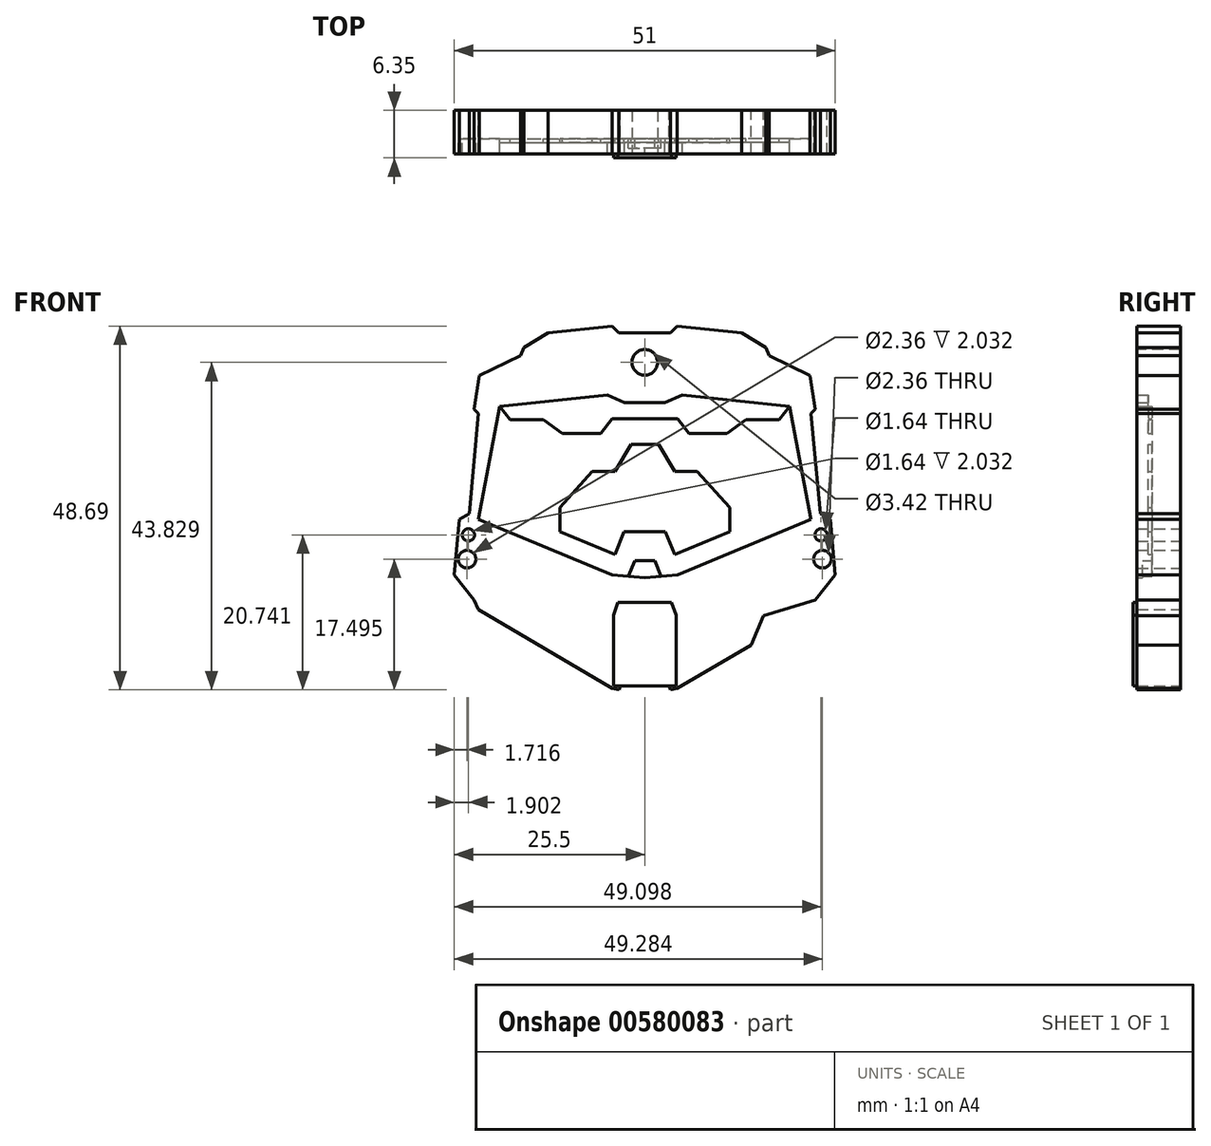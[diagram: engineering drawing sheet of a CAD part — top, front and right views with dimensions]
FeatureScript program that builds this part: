
annotation { "Feature Type Name" : "Feature", "Feature Type Description" : "" }
export const myFeature = defineFeature(function(context is Context, id is Id, definition is map)
    precondition{}
    {
        {
            var Q0;
            Q0=qCreatedBy(makeId("Front.planeOp"),FACE);
            var sketch = newSketch(context, id + "F0", { "sketchPlane" : qUnion([Q0])});
            skLineSegment(sketch, "E0", {"start": v(0, 26.6) * mm, "end": v(0, -24.2) * mm, "construction": true});
            skLineSegment(sketch, "E1", {"start": v(0, 26.6) * mm, "end": v(3.47, 26.6) * mm});
            skLineSegment(sketch, "E2", {"start": v(3.47, 26.6) * mm, "end": v(4.35, 27.52) * mm});
            skLineSegment(sketch, "E3", {"start": v(4.35, 27.52) * mm, "end": v(12.96, 26.6) * mm});
            skLineSegment(sketch, "E4", {"start": v(12.96, 26.6) * mm, "end": v(16.19, 24.61) * mm});
            skLineSegment(sketch, "E5", {"start": v(16.19, 24.61) * mm, "end": v(16.63, 23.54) * mm});
            skLineSegment(sketch, "E6", {"start": v(16.63, 23.54) * mm, "end": v(22.14, 20.88) * mm});
            skLineSegment(sketch, "E7", {"start": v(22.14, 20.88) * mm, "end": v(22.83, 16.39) * mm});
            skLineSegment(sketch, "E8", {"start": v(22.83, 16.39) * mm, "end": v(22.26, 15.82) * mm});
            skLineSegment(sketch, "E9", {"start": v(22.26, 15.82) * mm, "end": v(23.5, 2.4) * mm});
            skLineSegment(sketch, "E10", {"start": v(23.5, 2.4) * mm, "end": v(24.82, 1.66) * mm});
            skLineSegment(sketch, "E11", {"start": v(24.82, 1.66) * mm, "end": v(25.5, -5.75) * mm});
            skLineSegment(sketch, "E12", {"start": v(25.5, -5.75) * mm, "end": v(22.83, -9.12) * mm});
            skLineSegment(sketch, "E13", {"start": v(22.83, -9.12) * mm, "end": v(22.26, -10.43) * mm});
            skLineSegment(sketch, "E14", {"start": v(22.26, -10.43) * mm, "end": v(4.35, -20.92) * mm});
            skLineSegment(sketch, "E15", {"start": v(4.35, -20.92) * mm, "end": v(3.42, -21.17) * mm});
            skLineSegment(sketch, "E16", {"start": v(3.42, -21.17) * mm, "end": v(3.28, -20.63) * mm});
            skLineSegment(sketch, "E17", {"start": v(3.28, -20.63) * mm, "end": v(0, -20.63) * mm});
            skLineSegment(sketch, "E18.MirrorCS", {"start": v(-4.35, -20.92) * mm, "end": v(-3.42, -21.17) * mm});
            skLineSegment(sketch, "E19.MirrorCS", {"start": v(-3.42, -21.17) * mm, "end": v(-3.28, -20.63) * mm});
            skLineSegment(sketch, "E20.MirrorCS", {"start": v(-22.83, -9.12) * mm, "end": v(-22.26, -10.43) * mm});
            skLineSegment(sketch, "E21.MirrorCS", {"start": v(-23.5, 2.4) * mm, "end": v(-24.82, 1.66) * mm});
            skLineSegment(sketch, "E22.MirrorCS", {"start": v(-3.47, 26.6) * mm, "end": v(-4.35, 27.52) * mm});
            skLineSegment(sketch, "E23.MirrorCS", {"start": v(-16.19, 24.61) * mm, "end": v(-16.63, 23.54) * mm});
            skLineSegment(sketch, "E24.MirrorCS", {"start": v(-22.83, 16.39) * mm, "end": v(-22.26, 15.82) * mm});
            skLineSegment(sketch, "E25.MirrorCS", {"start": v(-22.26, -10.43) * mm, "end": v(-4.35, -20.92) * mm});
            skLineSegment(sketch, "E26.MirrorCS", {"start": v(-25.5, -5.75) * mm, "end": v(-22.83, -9.12) * mm});
            skLineSegment(sketch, "E27.MirrorCS", {"start": v(-24.82, 1.66) * mm, "end": v(-25.5, -5.75) * mm});
            skLineSegment(sketch, "E28.MirrorCS", {"start": v(-22.26, 15.82) * mm, "end": v(-23.5, 2.4) * mm});
            skLineSegment(sketch, "E29.MirrorCS", {"start": v(-4.35, 27.52) * mm, "end": v(-12.96, 26.6) * mm});
            skLineSegment(sketch, "E30.MirrorCS", {"start": v(-12.96, 26.6) * mm, "end": v(-16.19, 24.61) * mm});
            skLineSegment(sketch, "E31.MirrorCS", {"start": v(-16.63, 23.54) * mm, "end": v(-22.14, 20.88) * mm});
            skLineSegment(sketch, "E32.MirrorCS", {"start": v(-22.14, 20.88) * mm, "end": v(-22.83, 16.39) * mm});
            skLineSegment(sketch, "E33.MirrorCS", {"start": v(0, 26.6) * mm, "end": v(-3.47, 26.6) * mm});
            skLineSegment(sketch, "E34.MirrorCS", {"start": v(-3.28, -20.63) * mm, "end": v(0, -20.63) * mm});
            skLineSegment(sketch, "E35", {"start": v(-14.22, -15.15) * mm, "end": v(-15.87, -11.25) * mm});
            skLineSegment(sketch, "E36", {"start": v(-15.87, -11.25) * mm, "end": v(-22.83, -9.12) * mm});
            skLineSegment(sketch, "E37", {"start": v(-24.82, 1.66) * mm, "end": v(24.82, 1.66) * mm, "construction": true});
            skLineSegment(sketch, "E38", {"start": v(-22.14, 20.88) * mm, "end": v(-5, 22.7) * mm});
            skLineSegment(sketch, "E39", {"start": v(-5, 22.7) * mm, "end": v(-2.7, 21.68) * mm});
            skLineSegment(sketch, "E40", {"start": v(-2.7, 21.68) * mm, "end": v(0, 21.68) * mm});
            skLineSegment(sketch, "E41", {"start": v(-22.83, 16.39) * mm, "end": v(-5, 18.28) * mm});
            skLineSegment(sketch, "E42", {"start": v(-5, 18.28) * mm, "end": v(-2.7, 17.27) * mm});
            skLineSegment(sketch, "E43", {"start": v(-2.7, 17.27) * mm, "end": v(0, 17.27) * mm});
            skLineSegment(sketch, "E44", {"start": v(-19.4, 16.75) * mm, "end": v(-22.26, 1.66) * mm});
            skLineSegment(sketch, "E45", {"start": v(-22.26, 1.66) * mm, "end": v(-4.4, -5.75) * mm});
            skLineSegment(sketch, "E46", {"start": v(-4.4, -5.75) * mm, "end": v(0, -6.16) * mm});
            skLineSegment(sketch, "E47", {"start": v(-2.2, -5.96) * mm, "end": v(-1.33, -3.87) * mm});
            skLineSegment(sketch, "E48", {"start": v(-1.33, -3.87) * mm, "end": v(0, -3.87) * mm});
            skLineSegment(sketch, "E49", {"start": v(-4.35, -20.92) * mm, "end": v(-4.18, -20.63) * mm});
            skLineSegment(sketch, "E50", {"start": v(-4.18, -20.63) * mm, "end": v(-3.28, -20.63) * mm});
            skLineSegment(sketch, "E51", {"start": v(-12.03, -15.15) * mm, "end": v(-6.88, -10.3) * mm});
            skLineSegment(sketch, "E52", {"start": v(-6.88, -10.3) * mm, "end": v(-4.18, -11.2) * mm});
            skLineSegment(sketch, "E53", {"start": v(-4.18, -11.2) * mm, "end": v(-4.18, -20.63) * mm});
            skLineSegment(sketch, "E54", {"start": v(-4.18, -11.2) * mm, "end": v(-3.6, -9.47) * mm});
            skLineSegment(sketch, "E55", {"start": v(-3.6, -9.47) * mm, "end": v(0, -9.47) * mm});
            skLineSegment(sketch, "E56", {"start": v(-3.6, -9.47) * mm, "end": v(-6.5, -8.26) * mm});
            skLineSegment(sketch, "E57", {"start": v(-23.5, 2.4) * mm, "end": v(-22.26, 1.66) * mm});
            skLineSegment(sketch, "E58", {"start": v(-24.82, 1.66) * mm, "end": v(-22.26, 1.66) * mm});
            skLineSegment(sketch, "E59", {"start": v(-22.26, 1.66) * mm, "end": v(-22.26, -6.84) * mm});
            skLineSegment(sketch, "E60", {"start": v(-22.26, -6.84) * mm, "end": v(-22.83, -9.12) * mm});
            skCircle(sketch, "E61", {"center": v(-23.6, -0.43) * mm, "radius": 0.82 * mm});
            skCircle(sketch, "E62", {"center": v(-23.78, -3.68) * mm, "radius": 1.18 * mm});
            skLineSegment(sketch, "E63", {"start": v(-19.4, 16.75) * mm, "end": v(-18.01, 15.01) * mm});
            skLineSegment(sketch, "E64", {"start": v(-18.01, 15.01) * mm, "end": v(-13.57, 15.01) * mm});
            skLineSegment(sketch, "E65", {"start": v(-13.57, 15.01) * mm, "end": v(-11.01, 13.13) * mm});
            skLineSegment(sketch, "E66", {"start": v(-11.01, 13.13) * mm, "end": v(-5.9, 13.13) * mm});
            skLineSegment(sketch, "E67", {"start": v(-5.9, 13.13) * mm, "end": v(-4.4, 15.09) * mm});
            skLineSegment(sketch, "E68", {"start": v(-4.4, 15.09) * mm, "end": v(0, 15.09) * mm});
            skLineSegment(sketch, "E69", {"start": v(-4.02, -3.05) * mm, "end": v(-2.75, 0) * mm});
            skLineSegment(sketch, "E70", {"start": v(-2.75, 0) * mm, "end": v(0, 0) * mm});
            skLineSegment(sketch, "E71", {"start": v(-4.02, -3.05) * mm, "end": v(-11.36, 0) * mm});
            skLineSegment(sketch, "E72", {"start": v(-11.36, 0) * mm, "end": v(-11.36, 3.27) * mm});
            skLineSegment(sketch, "E73", {"start": v(-11.36, 3.27) * mm, "end": v(-7.03, 8.09) * mm});
            skLineSegment(sketch, "E74", {"start": v(-7.03, 8.09) * mm, "end": v(-4.02, 8.09) * mm});
            skLineSegment(sketch, "E75", {"start": v(-4.02, 8.09) * mm, "end": v(-1.83, 11.7) * mm});
            skLineSegment(sketch, "E76", {"start": v(-1.83, 11.7) * mm, "end": v(0, 11.7) * mm});
            skLineSegment(sketch, "E77.MirrorCS", {"start": v(4.35, -20.92) * mm, "end": v(4.18, -20.63) * mm});
            skLineSegment(sketch, "E78.MirrorCS", {"start": v(4.18, -20.63) * mm, "end": v(3.28, -20.63) * mm});
            skLineSegment(sketch, "E79.MirrorCS", {"start": v(24.82, 1.66) * mm, "end": v(22.26, 1.66) * mm});
            skLineSegment(sketch, "E80.MirrorCS", {"start": v(23.5, 2.4) * mm, "end": v(22.26, 1.66) * mm});
            skLineSegment(sketch, "E81.MirrorCS", {"start": v(22.26, -6.84) * mm, "end": v(22.83, -9.12) * mm});
            skLineSegment(sketch, "E82.MirrorCS", {"start": v(4.18, -11.2) * mm, "end": v(3.6, -9.47) * mm});
            skLineSegment(sketch, "E83.MirrorCS", {"start": v(3.6, -9.47) * mm, "end": v(0, -9.47) * mm});
            skLineSegment(sketch, "E84.MirrorCS", {"start": v(5, 18.28) * mm, "end": v(2.7, 17.27) * mm});
            skLineSegment(sketch, "E85.MirrorCS", {"start": v(7.03, 8.09) * mm, "end": v(4.02, 8.09) * mm});
            skLineSegment(sketch, "E86.MirrorCS", {"start": v(5.9, 13.13) * mm, "end": v(4.4, 15.09) * mm});
            skLineSegment(sketch, "E87.MirrorCS", {"start": v(2.75, 0) * mm, "end": v(0, 0) * mm});
            skLineSegment(sketch, "E88.MirrorCS", {"start": v(5, 22.7) * mm, "end": v(2.7, 21.68) * mm});
            skLineSegment(sketch, "E89.MirrorCS", {"start": v(19.4, 16.75) * mm, "end": v(18.01, 15.01) * mm});
            skLineSegment(sketch, "E90.MirrorCS", {"start": v(4.4, 15.09) * mm, "end": v(0, 15.09) * mm});
            skLineSegment(sketch, "E91.MirrorCS", {"start": v(6.88, -10.3) * mm, "end": v(4.18, -11.2) * mm});
            skLineSegment(sketch, "E92.MirrorCS", {"start": v(18.01, 15.01) * mm, "end": v(13.57, 15.01) * mm});
            skLineSegment(sketch, "E93.MirrorCS", {"start": v(4.4, -5.75) * mm, "end": v(0, -6.16) * mm});
            skLineSegment(sketch, "E94.MirrorCS", {"start": v(4.02, -3.05) * mm, "end": v(2.75, 0) * mm});
            skLineSegment(sketch, "E95.MirrorCS", {"start": v(11.36, 0) * mm, "end": v(11.36, 3.27) * mm});
            skLineSegment(sketch, "E96.MirrorCS", {"start": v(3.6, -9.47) * mm, "end": v(6.5, -8.26) * mm});
            skLineSegment(sketch, "E97.MirrorCS", {"start": v(2.7, 21.68) * mm, "end": v(0, 21.68) * mm});
            skLineSegment(sketch, "E98.MirrorCS", {"start": v(2.7, 17.27) * mm, "end": v(0, 17.27) * mm});
            skLineSegment(sketch, "E99.MirrorCS", {"start": v(4.02, 8.09) * mm, "end": v(1.83, 11.7) * mm});
            skLineSegment(sketch, "E100.MirrorCS", {"start": v(13.57, 15.01) * mm, "end": v(11.01, 13.13) * mm});
            skCircle(sketch, "E101.MirrorC", {"center": v(23.78, -3.68) * mm, "radius": 1.18 * mm});
            skLineSegment(sketch, "E102.MirrorCS", {"start": v(22.26, 1.66) * mm, "end": v(22.26, -6.84) * mm});
            skLineSegment(sketch, "E103.MirrorCS", {"start": v(14.22, -15.15) * mm, "end": v(15.87, -11.25) * mm});
            skCircle(sketch, "E104.MirrorC", {"center": v(23.6, -0.43) * mm, "radius": 0.82 * mm});
            skLineSegment(sketch, "E105.MirrorCS", {"start": v(11.01, 13.13) * mm, "end": v(5.9, 13.13) * mm});
            skLineSegment(sketch, "E106.MirrorCS", {"start": v(11.36, 3.27) * mm, "end": v(7.03, 8.09) * mm});
            skLineSegment(sketch, "E107.MirrorCS", {"start": v(22.83, 16.39) * mm, "end": v(5, 18.28) * mm});
            skLineSegment(sketch, "E108.MirrorCS", {"start": v(4.02, -3.05) * mm, "end": v(11.36, 0) * mm});
            skLineSegment(sketch, "E109.MirrorCS", {"start": v(22.26, 1.66) * mm, "end": v(4.4, -5.75) * mm});
            skLineSegment(sketch, "E110.MirrorCS", {"start": v(15.87, -11.25) * mm, "end": v(22.83, -9.12) * mm});
            skLineSegment(sketch, "E111.MirrorCS", {"start": v(19.4, 16.75) * mm, "end": v(22.26, 1.66) * mm});
            skLineSegment(sketch, "E112.MirrorCS", {"start": v(22.14, 20.88) * mm, "end": v(5, 22.7) * mm});
            skLineSegment(sketch, "E113.MirrorCS", {"start": v(12.03, -15.15) * mm, "end": v(6.88, -10.3) * mm});
            skLineSegment(sketch, "E114.MirrorCS", {"start": v(4.18, -11.2) * mm, "end": v(4.18, -20.63) * mm});
            skLineSegment(sketch, "E115.MirrorCS", {"start": v(24.82, 1.66) * mm, "end": v(-24.82, 1.66) * mm, "construction": true});
            skLineSegment(sketch, "E116.MirrorCS", {"start": v(1.33, -3.87) * mm, "end": v(0, -3.87) * mm});
            skLineSegment(sketch, "E117.MirrorCS", {"start": v(2.2, -5.96) * mm, "end": v(1.33, -3.87) * mm});
            skLineSegment(sketch, "E118.MirrorCS", {"start": v(1.83, 11.7) * mm, "end": v(0, 11.7) * mm});
            skLineSegment(sketch, "E119", {"start": v(-19.4, 16.75) * mm, "end": v(-22.26, 15.82) * mm});
            skLineSegment(sketch, "E120", {"start": v(19.4, 16.75) * mm, "end": v(22.26, 15.82) * mm});
            skSolve(sketch);
        }
        {
            var Q0;
            Q0=makeQuery(id+"F0.imprint","IMPRINT",FACE,{"disambiguationData":[TD([[makeQuery(id+"F0.imprint","IMPRINT",EDGE,{"derivedFrom":sQuery(id+"F0.wireOp",EDGE,"E18.MirrorCS")}),1.0]])]});
            var Q1;
            Q1=makeQuery(id+"F0.imprint","IMPRINT",FACE,{"disambiguationData":[TD([[makeQuery(id+"F0.imprint","IMPRINT",EDGE,{"derivedFrom":sQuery(id+"F0.wireOp",EDGE,"E16")}),-1.0]])]});
            var Q2;
            {var subQ1=sQuery(id+"F0.wireOp",EDGE,"E35");Q2=makeQuery(id+"F0.imprint","IMPRINT",FACE,{"disambiguationData":[TD([[makeQuery(id+"F0.imprint","IMPRINT",EDGE,{"derivedFrom":subQ1}),-1.0]])]});}
            var Q3;
            {var subQ0=sQuery(id+"F0.wireOp",EDGE,"E20.MirrorCS");Q3=makeQuery(id+"F0.imprint","IMPRINT",FACE,{"disambiguationData":[TD([[makeQuery(id+"F0.imprint","IMPRINT",EDGE,{"derivedFrom":subQ0}),1.0]])]});}
            var Q4;
            {var subQ0=sQuery(id+"F0.wireOp",EDGE,"E13");Q4=makeQuery(id+"F0.imprint","IMPRINT",FACE,{"disambiguationData":[TD([[makeQuery(id+"F0.imprint","IMPRINT",EDGE,{"derivedFrom":subQ0}),-1.0]])]});}
            var Q5;
            Q5=makeQuery(id+"F0.imprint","IMPRINT",FACE,{"disambiguationData":[TD([[makeQuery(id+"F0.imprint","IMPRINT",EDGE,{"derivedFrom":sQuery(id+"F0.wireOp",EDGE,"E79.MirrorCS")}),1.0]])]});
            var Q6;
            Q6=makeQuery(id+"F0.imprint","IMPRINT",FACE,{"disambiguationData":[TD([[makeQuery(id+"F0.imprint","IMPRINT",EDGE,{"derivedFrom":sQuery(id+"F0.wireOp",EDGE,"E26.MirrorCS")}),1.0]])]});
            var Q7;
            Q7=makeQuery(id+"F0.imprint","IMPRINT",FACE,{"disambiguationData":[TD([[makeQuery(id+"F0.imprint","IMPRINT",EDGE,{"derivedFrom":sQuery(id+"F0.wireOp",EDGE,"E28.MirrorCS")}),1.0]])]});
            var Q8;
            Q8=makeQuery(id+"F0.imprint","IMPRINT",FACE,{"disambiguationData":[TD([[makeQuery(id+"F0.imprint","IMPRINT",EDGE,{"derivedFrom":sQuery(id+"F0.wireOp",EDGE,"E80.MirrorCS")}),-1.0]])]});
            var Q9;
            Q9=makeQuery(id+"F0.imprint","IMPRINT",FACE,{"disambiguationData":[TD([[makeQuery(id+"F0.imprint","IMPRINT",EDGE,{"derivedFrom":sQuery(id+"F0.wireOp",EDGE,"E79.MirrorCS")}),-1.0]])]});
            var Q10;
            Q10=makeQuery(id+"F0.imprint","IMPRINT",FACE,{"disambiguationData":[TD([[makeQuery(id+"F0.imprint","IMPRINT",EDGE,{"derivedFrom":sQuery(id+"F0.wireOp",EDGE,"E21.MirrorCS")}),1.0]])]});
            var Q11;
            {var subQ0=sQuery(id+"F0.wireOp",EDGE,"E24.MirrorCS");Q11=makeQuery(id+"F0.imprint","IMPRINT",FACE,{"disambiguationData":[TD([[makeQuery(id+"F0.imprint","IMPRINT",EDGE,{"derivedFrom":subQ0}),1.0]])]});}
            var Q12;
            {var subQ0=sQuery(id+"F0.wireOp",EDGE,"E8");Q12=makeQuery(id+"F0.imprint","IMPRINT",FACE,{"disambiguationData":[TD([[makeQuery(id+"F0.imprint","IMPRINT",EDGE,{"derivedFrom":subQ0}),-1.0]])]});}
            var Q13;
            {var subQ4=sQuery(id+"F0.wireOp",EDGE,"E32.MirrorCS");Q13=makeQuery(id+"F0.imprint","IMPRINT",FACE,{"disambiguationData":[TD([[makeQuery(id+"F0.imprint","IMPRINT",EDGE,{"derivedFrom":subQ4}),1.0]])]});}
            var Q14;
            Q14=makeQuery(id+"F0.imprint","IMPRINT",FACE,{"disambiguationData":[TD([[makeQuery(id+"F0.imprint","IMPRINT",EDGE,{"derivedFrom":sQuery(id+"F0.wireOp",EDGE,"E22.MirrorCS")}),1.0]])]});
            extrude(context, id + "F1", {"entities" : qUnion([Q0, Q1, Q2, Q3, Q4, Q5, Q6, Q7, Q8, Q9, Q10, Q11, Q12, Q13, Q14]), "depth" : 5.84 * mm});
        }
        {
            var Q0;
            Q0=makeQuery(id+"F0.imprint","IMPRINT",FACE,{"disambiguationData":[TD([[makeQuery(id+"F0.imprint","IMPRINT",EDGE,{"derivedFrom":sQuery(id+"F0.wireOp",EDGE,"E101.MirrorC")}),-1.0]])]});
            var Q1;
            Q1=makeQuery(id+"F0.imprint","IMPRINT",FACE,{"disambiguationData":[TD([[makeQuery(id+"F0.imprint","IMPRINT",EDGE,{"derivedFrom":sQuery(id+"F0.wireOp",EDGE,"E104.MirrorC")}),-1.0]])]});
            var Q2;
            Q2=makeQuery(id+"F0.imprint","IMPRINT",FACE,{"disambiguationData":[TD([[makeQuery(id+"F0.imprint","IMPRINT",EDGE,{"derivedFrom":sQuery(id+"F0.wireOp",EDGE,"E62")}),1.0]])]});
            var Q3;
            Q3=makeQuery(id+"F0.imprint","IMPRINT",FACE,{"disambiguationData":[TD([[makeQuery(id+"F0.imprint","IMPRINT",EDGE,{"derivedFrom":sQuery(id+"F0.wireOp",EDGE,"E61")}),1.0]])]});
            var Q4;
            Q4=makeQuery(id+"F0.imprint","IMPRINT",FACE,{"disambiguationData":[TD([[makeQuery(id+"F0.imprint","IMPRINT",EDGE,{"derivedFrom":sQuery(id+"F0.wireOp",EDGE,"E44")}),1.0]])]});
            extrude(context, id + "F2", {"entities" : qUnion([Q0, Q1, Q2, Q3, Q4]), "operationType" : NewBodyOperationType.ADD, "depth" : 3.8 * mm});
        }
        {
            var Q0;
            {var subQ4=sQuery(id+"F0.wireOp",EDGE,"E47");Q0=makeQuery(id+"F0.imprint","IMPRINT",FACE,{"disambiguationData":[TD([[makeQuery(id+"F0.imprint","IMPRINT",EDGE,{"derivedFrom":subQ4}),-1.0]])]});}
            extrude(context, id + "F3", {"entities" : qUnion([Q0]), "operationType" : NewBodyOperationType.ADD, "depth" : 5.08 * mm});
        }
        {
            var Q0;
            Q0=makeQuery(id+"F0.imprint","IMPRINT",FACE,{"disambiguationData":[TD([[makeQuery(id+"F0.imprint","IMPRINT",EDGE,{"derivedFrom":sQuery(id+"F0.wireOp",EDGE,"E69")}),1.0]])]});
            var Q1;
            {var subQ1=sQuery(id+"F0.wireOp",EDGE,"E42");Q1=makeQuery(id+"F0.imprint","IMPRINT",FACE,{"disambiguationData":[TD([[makeQuery(id+"F0.imprint","IMPRINT",EDGE,{"derivedFrom":subQ1}),-1.0]])]});}
            extrude(context, id + "F4", {"entities" : qUnion([Q0, Q1]), "operationType" : NewBodyOperationType.ADD, "depth" : 4.32 * mm});
        }
        {
            var Q0;
            Q0=makeQuery(id+"F1.opExtrude","CAP_FACE",FACE,{"disambiguationData":[OSD([sQuery(id+"F0.wireOp",EDGE,"E18.MirrorCS"),sQuery(id+"F0.wireOp",EDGE,"E19.MirrorCS"),sQuery(id+"F0.wireOp",EDGE,"E20.MirrorCS"),sQuery(id+"F0.wireOp",EDGE,"E21.MirrorCS"),sQuery(id+"F0.wireOp",EDGE,"E22.MirrorCS"),sQuery(id+"F0.wireOp",EDGE,"E23.MirrorCS"),sQuery(id+"F0.wireOp",EDGE,"E24.MirrorCS"),sQuery(id+"F0.wireOp",EDGE,"E25.MirrorCS"),sQuery(id+"F0.wireOp",EDGE,"E26.MirrorCS"),sQuery(id+"F0.wireOp",EDGE,"E27.MirrorCS"),sQuery(id+"F0.wireOp",EDGE,"E28.MirrorCS"),sQuery(id+"F0.wireOp",EDGE,"E29.MirrorCS"),sQuery(id+"F0.wireOp",EDGE,"E30.MirrorCS"),sQuery(id+"F0.wireOp",EDGE,"E31.MirrorCS"),sQuery(id+"F0.wireOp",EDGE,"E32.MirrorCS"),sQuery(id+"F0.wireOp",EDGE,"E33.MirrorCS"),sQuery(id+"F0.wireOp",EDGE,"E34.MirrorCS"),sQuery(id+"F0.wireOp",EDGE,"E41"),sQuery(id+"F0.wireOp",EDGE,"E42"),sQuery(id+"F0.wireOp",EDGE,"E43"),sQuery(id+"F0.wireOp",EDGE,"E44"),sQuery(id+"F0.wireOp",EDGE,"E45"),sQuery(id+"F0.wireOp",EDGE,"E46"),sQuery(id+"F0.wireOp",EDGE,"E61"),sQuery(id+"F0.wireOp",EDGE,"E62"),sQuery(id+"F0.wireOp",EDGE,"E16"),sQuery(id+"F0.wireOp",EDGE,"E17"),sQuery(id+"F0.wireOp",EDGE,"E15"),sQuery(id+"F0.wireOp",EDGE,"E10"),sQuery(id+"F0.wireOp",EDGE,"E13"),sQuery(id+"F0.wireOp",EDGE,"E8"),sQuery(id+"F0.wireOp",EDGE,"E84.MirrorCS"),sQuery(id+"F0.wireOp",EDGE,"E12"),sQuery(id+"F0.wireOp",EDGE,"E2"),sQuery(id+"F0.wireOp",EDGE,"E1"),sQuery(id+"F0.wireOp",EDGE,"E93.MirrorCS"),sQuery(id+"F0.wireOp",EDGE,"E4"),sQuery(id+"F0.wireOp",EDGE,"E98.MirrorCS"),sQuery(id+"F0.wireOp",EDGE,"E5"),sQuery(id+"F0.wireOp",EDGE,"E101.MirrorC"),sQuery(id+"F0.wireOp",EDGE,"E11"),sQuery(id+"F0.wireOp",EDGE,"E104.MirrorC"),sQuery(id+"F0.wireOp",EDGE,"E14"),sQuery(id+"F0.wireOp",EDGE,"E107.MirrorCS"),sQuery(id+"F0.wireOp",EDGE,"E109.MirrorCS"),sQuery(id+"F0.wireOp",EDGE,"E3"),sQuery(id+"F0.wireOp",EDGE,"E6"),sQuery(id+"F0.wireOp",EDGE,"E111.MirrorCS"),sQuery(id+"F0.wireOp",EDGE,"E9"),sQuery(id+"F0.wireOp",EDGE,"E7")])],"isStart":false});
            var sketch = newSketch(context, id + "F5", { "sketchPlane" : qUnion([Q0])});
            skCircle(sketch, "E121", {"center": v(0, 22.66) * mm, "radius": 1.71 * mm});
            skSolve(sketch);
        }
        {
            var Q0;
            Q0=qSketchRegion(id+"F5",true);
            extrude(context, id + "F6", {"entities" : qUnion([Q0]), "operationType" : NewBodyOperationType.REMOVE, "oppositeDirection" : true, "depth" : 25.4 * mm, "offsetDistance" : 25.4 * mm});
        }
        {
            var Q0;
            Q0=makeQuery(id+"F0.imprint","IMPRINT",FACE,{"disambiguationData":[TD([[makeQuery(id+"F0.imprint","IMPRINT",EDGE,{"derivedFrom":sQuery(id+"F0.wireOp",EDGE,"E34.MirrorCS")}),1.0]])]});
            extrude(context, id + "F7", {"entities" : qUnion([Q0]), "operationType" : NewBodyOperationType.ADD, "depth" : 6.35 * mm});
        }
    });
